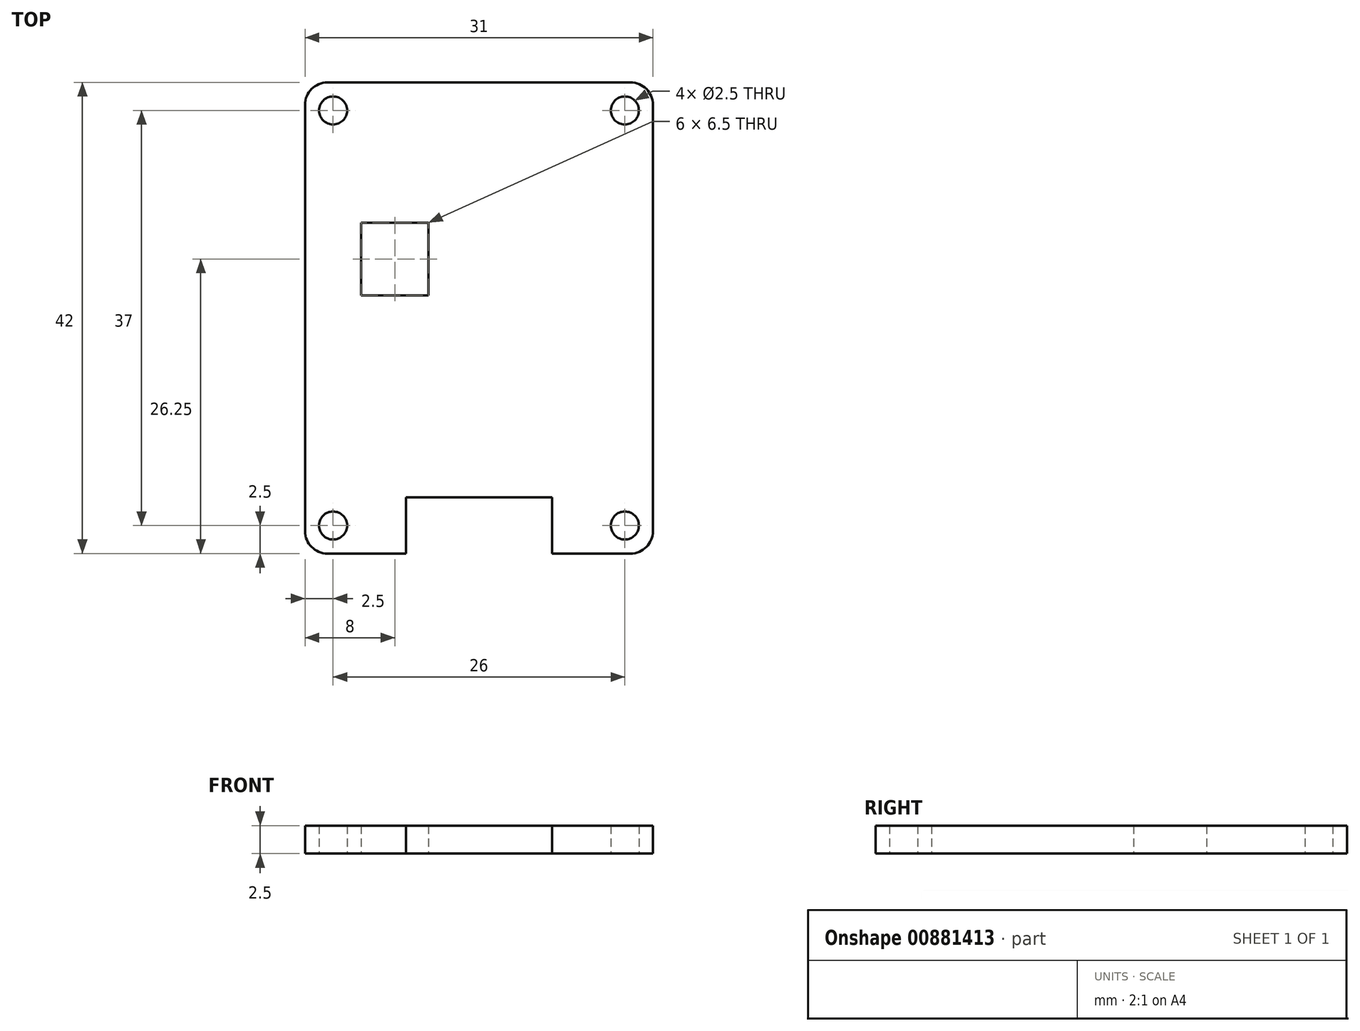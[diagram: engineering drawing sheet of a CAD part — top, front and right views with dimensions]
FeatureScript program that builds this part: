
annotation { "Feature Type Name" : "Feature", "Feature Type Description" : "" }
export const myFeature = defineFeature(function(context is Context, id is Id, definition is map)
    precondition{}
    {
        {
            var Q0;
            Q0=qCreatedBy(makeId("Top.planeOp"),FACE);
            var sketch = newSketch(context, id + "F0", { "sketchPlane" : qUnion([Q0])});
            skLineSegment(sketch, "E0.bottom", {"start": v(10.5, -16) * mm, "end": v(-10.5, -16) * mm});
            skLineSegment(sketch, "E0.top", {"start": v(10.5, 16) * mm, "end": v(-10.5, 16) * mm});
            skLineSegment(sketch, "E0.left", {"start": v(10.5, -16) * mm, "end": v(10.5, 16) * mm});
            skLineSegment(sketch, "E0.right", {"start": v(-10.5, -16) * mm, "end": v(-10.5, 16) * mm});
            skPoint(sketch, "E0.middle", {"position": v(0, 0) * mm});
            skLineSegment(sketch, "E1.0", {"start": v(15.5, 21) * mm, "end": v(-15.5, 21) * mm});
            skLineSegment(sketch, "E1.1", {"start": v(15.5, -21) * mm, "end": v(15.5, 21) * mm});
            skLineSegment(sketch, "E1.2", {"start": v(15.5, -21) * mm, "end": v(-15.5, -21) * mm});
            skLineSegment(sketch, "E1.3", {"start": v(-15.5, -21) * mm, "end": v(-15.5, 21) * mm});
            skPoint(sketch, "E2", {"position": v(13, 18.5) * mm});
            skPoint(sketch, "E3", {"position": v(-13, 18.5) * mm});
            skPoint(sketch, "E4", {"position": v(-13, -18.5) * mm});
            skPoint(sketch, "E5", {"position": v(13, -18.5) * mm});
            skCircle(sketch, "E6", {"center": v(-13, -18.5) * mm, "radius": 1.25 * mm});
            skCircle(sketch, "E7", {"center": v(13, -18.5) * mm, "radius": 1.25 * mm});
            skCircle(sketch, "E8", {"center": v(13, 18.5) * mm, "radius": 1.25 * mm});
            skCircle(sketch, "E9", {"center": v(-13, 18.5) * mm, "radius": 1.25 * mm});
            skPoint(sketch, "E10", {"position": v(-10.5, 8.5) * mm});
            skPoint(sketch, "E11", {"position": v(-10.5, 2) * mm});
            skPoint(sketch, "E12", {"position": v(-4.5, 8.5) * mm});
            skPoint(sketch, "E13", {"position": v(-4.5, 2) * mm});
            skLineSegment(sketch, "E14", {"start": v(-10.5, 8.5) * mm, "end": v(-4.5, 8.5) * mm});
            skLineSegment(sketch, "E15", {"start": v(-4.5, 8.5) * mm, "end": v(-4.5, 2) * mm});
            skLineSegment(sketch, "E16", {"start": v(-4.5, 2) * mm, "end": v(-10.5, 2) * mm});
            skPoint(sketch, "E17", {"position": v(6.5, -16) * mm});
            skPoint(sketch, "E18", {"position": v(-6.5, -16) * mm});
            skLineSegment(sketch, "E19", {"start": v(-6.5, -16) * mm, "end": v(-6.5, -21) * mm});
            skLineSegment(sketch, "E20", {"start": v(6.5, -16) * mm, "end": v(6.5, -21) * mm});
            skSolve(sketch);
        }
        {
            var Q0;
            {var subQ4=sQuery(id+"F0.wireOp",EDGE,"E0.bottom");Q0=makeQuery(id+"F0.imprint","IMPRINT",FACE,{"disambiguationData":[TD([[makeQuery(id+"F0.imprint","IMPRINT",EDGE,{"derivedFrom":subQ4}),1.0]])]});}
            var Q1;
            {var subQ1=sQuery(id+"F0.wireOp",EDGE,"E0.bottom");Q1=makeQuery(id+"F0.imprint","IMPRINT",FACE,{"disambiguationData":[TD([[makeQuery(id+"F0.imprint","IMPRINT",EDGE,{"derivedFrom":subQ1}),-1.0]])]});}
            extrude(context, id + "F1", {"entities" : qUnion([Q0, Q1]), "depth" : 2.5 * mm, "offsetDistance" : 25 * mm});
        }
        {
            var Q0;
            Q0=makeQuery(id+"F1.opExtrude","SWEPT_EDGE",EDGE,{"disambiguationData":[OSD([sQuery(id+"F0.wireOp",EDGE,"E1.0"),sQuery(id+"F0.wireOp",EDGE,"E1.3")])]});
            var Q1;
            Q1=makeQuery(id+"F1.opExtrude","SWEPT_EDGE",EDGE,{"disambiguationData":[OSD([sQuery(id+"F0.wireOp",EDGE,"E1.0"),sQuery(id+"F0.wireOp",EDGE,"E1.1")])]});
            var Q2;
            Q2=makeQuery(id+"F1.opExtrude","SWEPT_EDGE",EDGE,{"disambiguationData":[OSD([sQuery(id+"F0.wireOp",EDGE,"E1.1"),sQuery(id+"F0.wireOp",EDGE,"E1.2")])]});
            var Q3;
            Q3=makeQuery(id+"F1.opExtrude","SWEPT_EDGE",EDGE,{"disambiguationData":[OSD([sQuery(id+"F0.wireOp",EDGE,"E1.2"),sQuery(id+"F0.wireOp",EDGE,"E1.3")])]});
            fillet(context, id + "F2", {"entities" : qUnion([Q0, Q1, Q2, Q3]), "tangentPropagation" : true, "radius" : 2 * mm, "defaultsChanged" : true, "vertexSettings" : [], "allowEdgeOverflow" : false});
        }
    });
